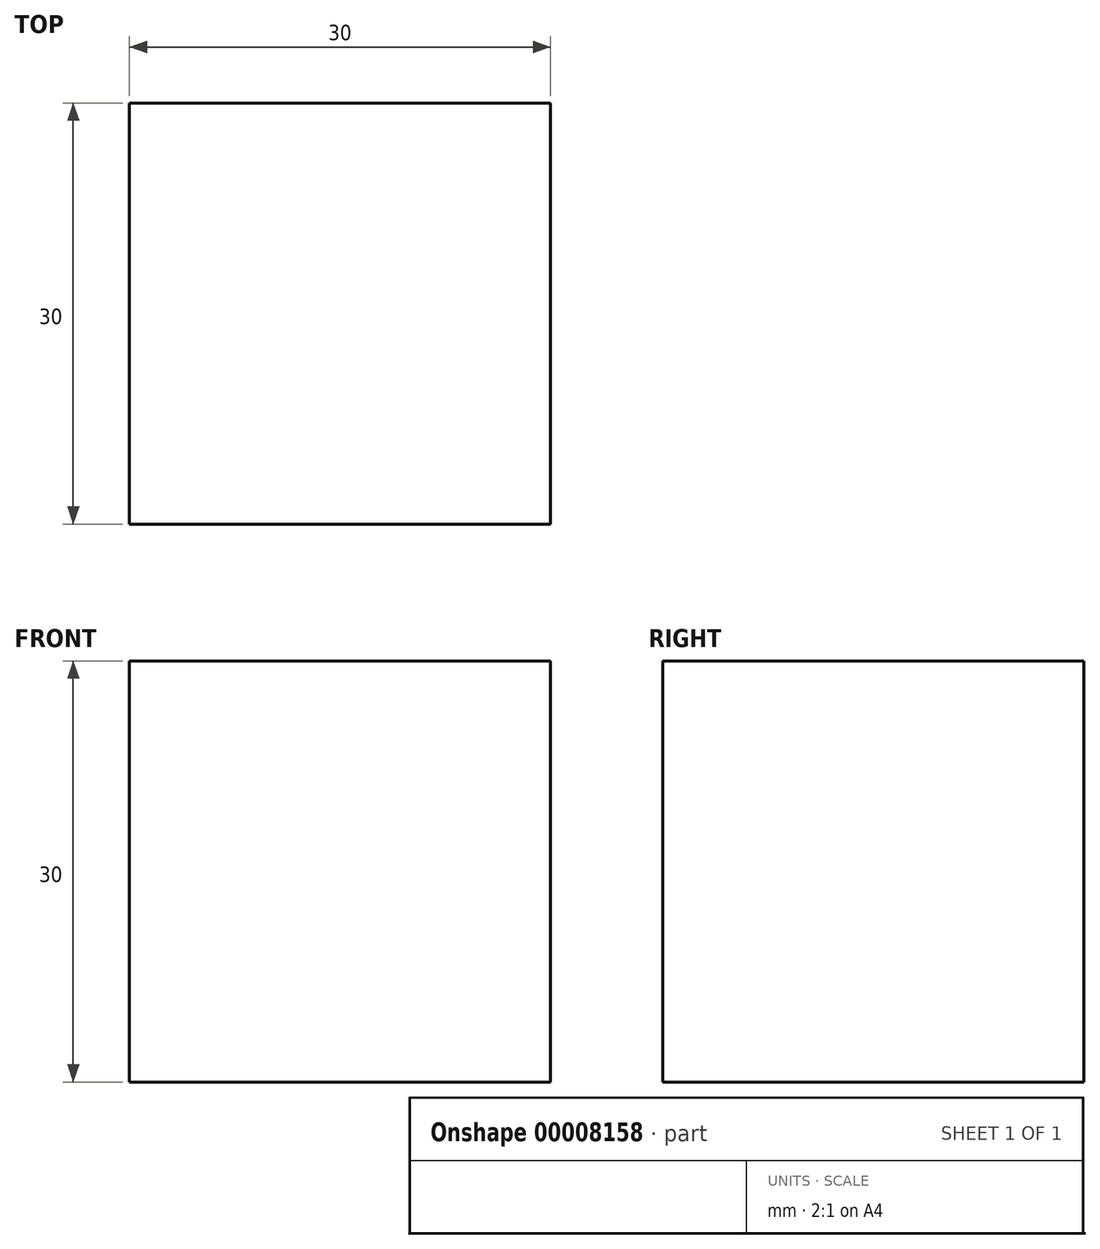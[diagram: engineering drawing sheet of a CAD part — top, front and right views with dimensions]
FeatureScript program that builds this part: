
annotation { "Feature Type Name" : "Feature", "Feature Type Description" : "" }
export const myFeature = defineFeature(function(context is Context, id is Id, definition is map)
    precondition{}
    {
        {
            var Q0;
            Q0=qCreatedBy(makeId("Top.planeOp"),FACE);
            var sketch = newSketch(context, id + "F0", { "sketchPlane" : qUnion([Q0])});
            skLineSegment(sketch, "E0.bottom", {"start": v(0, 0) * mm, "end": v(30, 0) * mm});
            skLineSegment(sketch, "E0.top", {"start": v(0, -30) * mm, "end": v(30, -30) * mm});
            skLineSegment(sketch, "E0.left", {"start": v(0, 0) * mm, "end": v(0, -30) * mm});
            skLineSegment(sketch, "E0.right", {"start": v(30, 0) * mm, "end": v(30, -30) * mm});
            skSolve(sketch);
        }
        {
            var Q0;
            Q0=qCreatedBy(makeId("Front.planeOp"),FACE);
            var sketch = newSketch(context, id + "F1", { "sketchPlane" : qUnion([Q0])});
            skLineSegment(sketch, "E1.0", {"start": v(0, 0) * mm, "end": v(30, 0) * mm});
            skLineSegment(sketch, "E2", {"start": v(0, 0) * mm, "end": v(0, 30) * mm});
            skLineSegment(sketch, "E3", {"start": v(0, 30) * mm, "end": v(30, 30) * mm});
            skLineSegment(sketch, "E4", {"start": v(30, 30) * mm, "end": v(30, 0) * mm});
            skSolve(sketch);
        }
        {
            var Q0;
            Q0=sQuery(id+"F0.wireOp",VERTEX,"E0.left.end");
            var Q1;
            Q1=qCreatedBy(makeId("Front.planeOp"),FACE);
            cPlane(context, id + "F2", {"entities" : qUnion([Q0, Q1]), "cplaneType" : CPlaneType.PLANE_POINT, "offset" : 150 * mm, "width" : 150 * mm, "height" : 150 * mm});
        }
        {
            var Q0;
            Q0=makeQuery(id+"F1.imprint","IMPRINT",FACE,{"disambiguationData":[TD([[makeQuery(id+"F1.imprint","IMPRINT",EDGE,{"derivedFrom":sQuery(id+"F1.wireOp",EDGE,"E1.0")}),1.0]])]});
            var Q1;
            Q1=qCreatedBy(id+"F2.planeOp",FACE);
            extrude(context, id + "F3", {"entities" : qUnion([Q0]), "endBound" : BoundingType.UP_TO_SURFACE, "endBoundEntityFace" : qUnion([Q1]), "depth" : 25 * mm});
        }
    });
